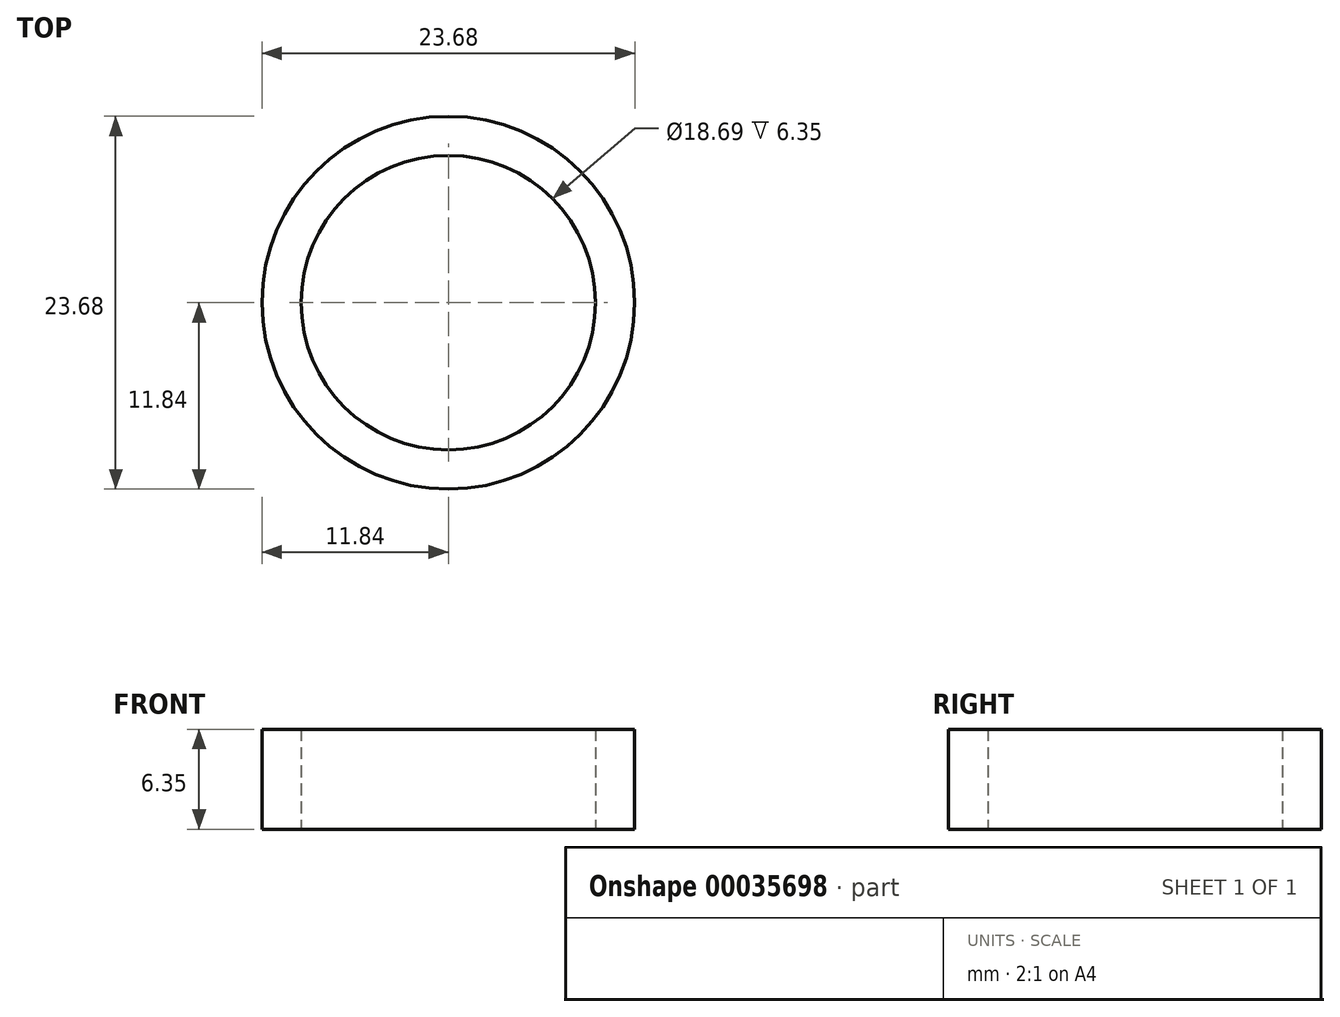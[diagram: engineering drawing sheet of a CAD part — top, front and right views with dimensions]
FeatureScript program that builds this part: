
annotation { "Feature Type Name" : "Feature", "Feature Type Description" : "" }
export const myFeature = defineFeature(function(context is Context, id is Id, definition is map)
    precondition{}
    {
        {
            var Q0;
            Q0=qCreatedBy(makeId("Front.planeOp"),FACE);
            var sketch = newSketch(context, id + "F0", { "sketchPlane" : qUnion([Q0])});
            skLineSegment(sketch, "E0", {"start": v(0, 0) * mm, "end": v(0, 6.35) * mm});
            skLineSegment(sketch, "E1", {"start": v(0, 6.35) * mm, "end": v(9.35, 6.35) * mm});
            skLineSegment(sketch, "E2", {"start": v(9.35, 6.35) * mm, "end": v(9.35, 0) * mm});
            skLineSegment(sketch, "E3", {"start": v(9.35, 0) * mm, "end": v(0, 0) * mm});
            skLineSegment(sketch, "E4", {"start": v(9.35, 6.35) * mm, "end": v(11.84, 6.35) * mm});
            skLineSegment(sketch, "E5", {"start": v(11.84, 6.35) * mm, "end": v(11.84, 0) * mm});
            skLineSegment(sketch, "E6", {"start": v(11.84, 0) * mm, "end": v(9.35, 0) * mm});
            skSolve(sketch);
        }
        {
            var Q0;
            Q0=makeQuery(id+"F0.imprint","IMPRINT",FACE,{"disambiguationData":[TD([[makeQuery(id+"F0.imprint","IMPRINT",EDGE,{"derivedFrom":sQuery(id+"F0.wireOp",EDGE,"E2")}),1.0]])]});
            var Q1;
            Q1=sQuery(id+"F0.wireOp",EDGE,"E0");
            revolve(context, id + "F1", {"entities" : qUnion([Q0]), "axis" : qUnion([Q1]), "revolveType" : RevolveType.FULL});
        }
    });
